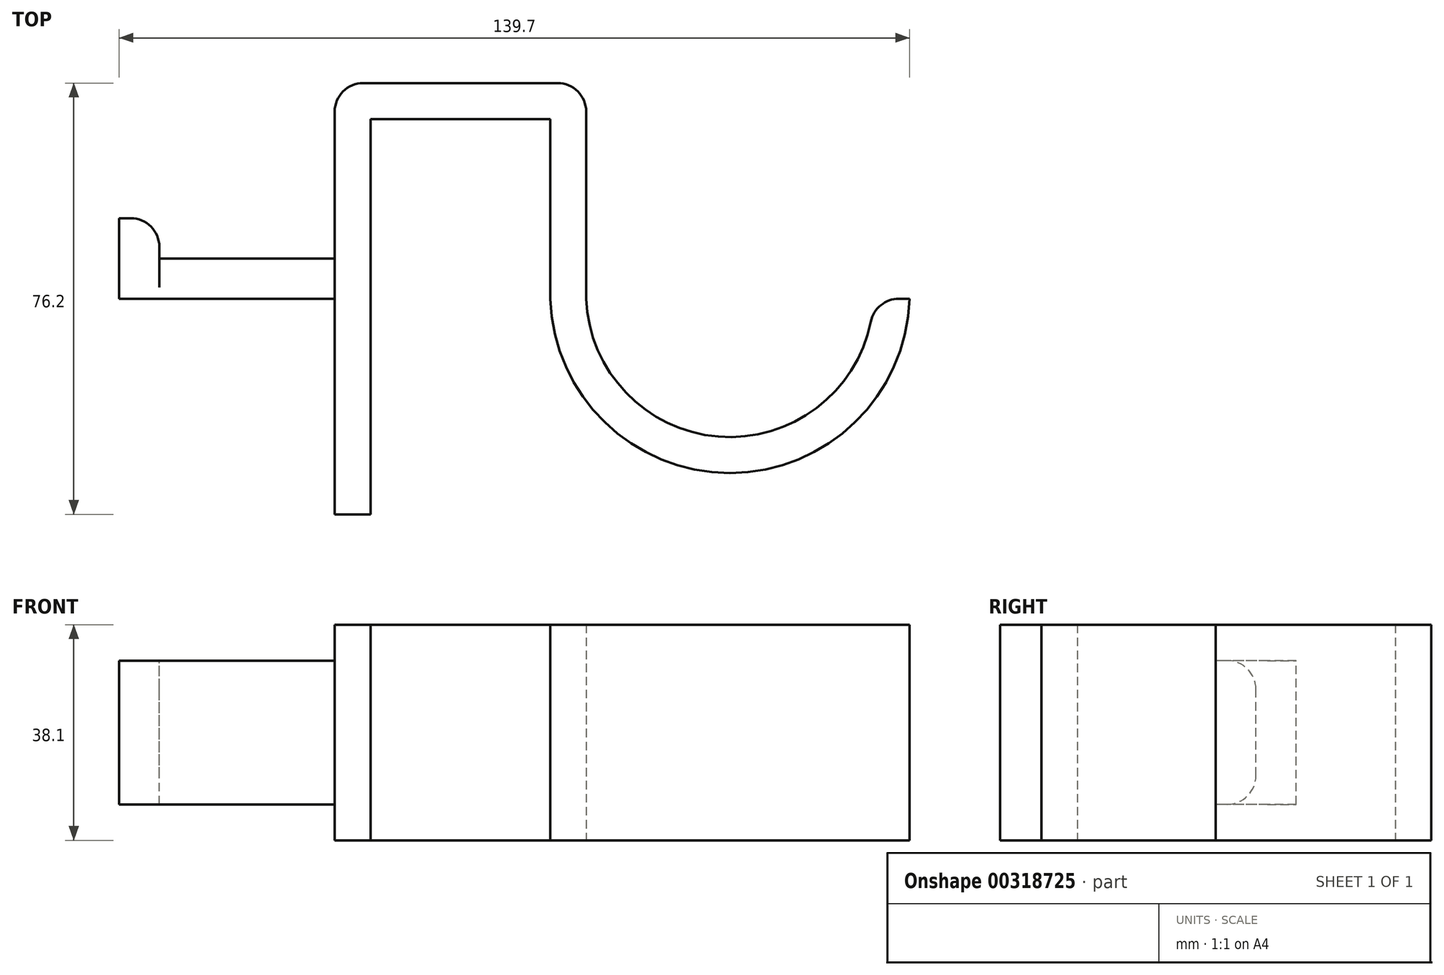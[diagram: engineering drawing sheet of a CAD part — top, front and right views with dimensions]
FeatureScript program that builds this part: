
annotation { "Feature Type Name" : "Feature", "Feature Type Description" : "" }
export const myFeature = defineFeature(function(context is Context, id is Id, definition is map)
    precondition{}
    {
        {
            var Q0;
            Q0=qCreatedBy(makeId("Top.planeOp"),FACE);
            var sketch = newSketch(context, id + "F0", { "sketchPlane" : qUnion([Q0])});
            skLineSegment(sketch, "E0", {"start": v(0, 0) * mm, "end": v(0, 76.2) * mm});
            skLineSegment(sketch, "E1", {"start": v(0, 76.2) * mm, "end": v(44.45, 76.2) * mm});
            skLineSegment(sketch, "E2", {"start": v(44.45, 76.2) * mm, "end": v(44.45, 38.1) * mm});
            skArc(sketch, "E3", {"start": v(44.45, 38.1) * mm, "mid": v(69.85, 13.65) * mm, "end": v(95.25, 38.1) * mm});
            skArc(sketch, "E4", {"start": v(38.1, 38.1) * mm, "mid": v(69.85, 7.3) * mm, "end": v(101.6, 38.1) * mm});
            skLineSegment(sketch, "E5", {"start": v(38.1, 38.1) * mm, "end": v(38.1, 69.85) * mm});
            skLineSegment(sketch, "E6", {"start": v(38.1, 69.85) * mm, "end": v(6.35, 69.85) * mm});
            skLineSegment(sketch, "E7", {"start": v(6.35, 69.85) * mm, "end": v(6.35, 0) * mm});
            skLineSegment(sketch, "E8", {"start": v(6.35, 0) * mm, "end": v(0, 0) * mm});
            skLineSegment(sketch, "E9", {"start": v(95.25, 38.1) * mm, "end": v(101.6, 38.1) * mm});
            skSolve(sketch);
        }
        {
            var Q0;
            Q0 = qSketchRegion(id + "F0", true);
            extrude(context, id + "F1", {"entities" : qUnion([Q0]), "depth" : 38.1 * mm, "offsetDistance" : 25.4 * mm});
        }
        {
            var Q0;
            Q0=makeQuery(id+"F1.opExtrude","SWEPT_EDGE",EDGE,{"disambiguationData":[OSD([sQuery(id+"F0.wireOp",EDGE,"E3"),sQuery(id+"F0.wireOp",EDGE,"E9")])]});
            fillet(context, id + "F2", {"entities" : qUnion([Q0]), "radius" : 5.08 * mm, "tangentPropagation" : true, "allowEdgeOverflow" : false});
        }
        {
            var Q0;
            Q0=makeQuery(id+"F1.opExtrude","SWEPT_EDGE",EDGE,{"disambiguationData":[OSD([sQuery(id+"F0.wireOp",EDGE,"E1"),sQuery(id+"F0.wireOp",EDGE,"E2")])]});
            var Q1;
            Q1=makeQuery(id+"F1.opExtrude","SWEPT_EDGE",EDGE,{"disambiguationData":[OSD([sQuery(id+"F0.wireOp",EDGE,"E0"),sQuery(id+"F0.wireOp",EDGE,"E1")])]});
            fillet(context, id + "F3", {"entities" : qUnion([Q0, Q1]), "radius" : 5.08 * mm, "tangentPropagation" : true, "allowEdgeOverflow" : false});
        }
        {
            var Q0;
            Q0=makeQuery(id+"F1.opExtrude","SWEPT_FACE",FACE,{"disambiguationData":[OSD([sQuery(id+"F0.wireOp",EDGE,"E0")])]});
            var sketch = newSketch(context, id + "F4", { "sketchPlane" : qUnion([Q0])});
            skLineSegment(sketch, "E10.bottom", {"start": v(-45.21, 6.35) * mm, "end": v(-38.1, 6.35) * mm});
            skLineSegment(sketch, "E10.top", {"start": v(-45.21, 31.75) * mm, "end": v(-38.1, 31.75) * mm});
            skLineSegment(sketch, "E10.left", {"start": v(-45.21, 6.35) * mm, "end": v(-45.21, 31.75) * mm});
            skLineSegment(sketch, "E10.right", {"start": v(-38.1, 6.35) * mm, "end": v(-38.1, 31.75) * mm});
            skSolve(sketch);
        }
        {
            var Q0;
            Q0 = qSketchRegion(id + "F4", true);
            extrude(context, id + "F5", {"entities" : qUnion([Q0]), "operationType" : NewBodyOperationType.ADD, "depth" : 38.1 * mm, "offsetDistance" : 25.4 * mm});
        }
        {
            var Q0;
            Q0=makeQuery(id+"F5.opExtrude","SWEPT_FACE",FACE,{"disambiguationData":[OSD([sQuery(id+"F4.wireOp",EDGE,"E10.left")])]});
            var sketch = newSketch(context, id + "F6", { "sketchPlane" : qUnion([Q0])});
            skLineSegment(sketch, "E11.bottom", {"start": v(38.1, 6.35) * mm, "end": v(30.99, 6.35) * mm});
            skLineSegment(sketch, "E11.top", {"start": v(38.1, 31.75) * mm, "end": v(30.99, 31.75) * mm});
            skLineSegment(sketch, "E11.left", {"start": v(38.1, 6.35) * mm, "end": v(38.1, 31.75) * mm});
            skLineSegment(sketch, "E11.right", {"start": v(30.99, 6.35) * mm, "end": v(30.99, 31.75) * mm});
            skSolve(sketch);
        }
        {
            var Q0;
            Q0 = qSketchRegion(id + "F6", true);
            extrude(context, id + "F7", {"entities" : qUnion([Q0]), "operationType" : NewBodyOperationType.ADD, "depth" : 7.11 * mm, "offsetDistance" : 25.4 * mm});
        }
        {
            var Q0;
            Q0=makeQuery(id+"F5.opExtrude","SWEPT_EDGE",EDGE,{"disambiguationData":[OSD([sQuery(id+"F4.wireOp",EDGE,"E10.top"),sQuery(id+"F4.wireOp",EDGE,"E10.left")])]});
            var Q1;
            Q1=makeQuery(id+"F5.opExtrude","SWEPT_EDGE",EDGE,{"disambiguationData":[OSD([sQuery(id+"F4.wireOp",EDGE,"E10.bottom"),sQuery(id+"F4.wireOp",EDGE,"E10.left")])]});
            var Q2;
            Q2=makeQuery(id+"F7.opExtrude","CAP_EDGE",EDGE,{"disambiguationData":[OSD([sQuery(id+"F6.wireOp",EDGE,"E11.right")])],"isStart":false});
            fillet(context, id + "F8", {"entities" : qUnion([Q0, Q1, Q2]), "radius" : 5.08 * mm, "tangentPropagation" : true, "allowEdgeOverflow" : false});
        }
    });
